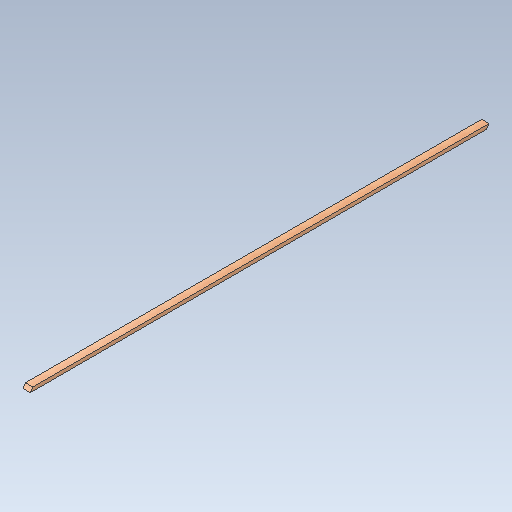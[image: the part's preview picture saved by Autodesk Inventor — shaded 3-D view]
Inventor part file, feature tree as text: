
AUTODESK INVENTOR PART (.ipt)
format: ipt  version: 2020.1 (Build 241239000, 239)  size: 265,216 bytes
history: native  units: mm
features: extrude x8, sketch x8, projected_geometry x7, other x7, fillet x4, reference x3
ambient origin geometry x8: Origin, YZ Plane, XZ Plane, XY Plane, X Axis, Y Axis, Z Axis, Center Point
bodies: Solid1 (feature_tree)
feature tree (37):
  extrude  "brædt"  Depth=80.0mm
  extrude  "spor til stål-håndfang"  Depth=40.0mm
  extrude  "spor til LED og liste"  Depth=4844.551mm
  extrude  "spor til ledninger"  Depth=5.0mm TaperAngle=0.0deg
  extrude  "endeafskær top"  Depth=6.3mm
  extrude  "endeafskær bund"  Depth=12.0mm TaperAngle=0.0deg
  fillet  "Fillet2"  Radius=1.0mm
  fillet  "Fillet3"  Radius=1.0mm
  fillet  "Fillet4"  Radius=10.0mm
  fillet  "Fillet5"  [1 undecoded]
  extrude  "pilothuller"  Depth=7.0mm TaperAngle=0.0deg
  extrude  "spor til acryl"  Depth=2.0mm
  sketch  "Sketch1"  dims[d5=5000.0mm d6=0.0mm d8=80.0mm]
  sketch  "Sketch2"  dims[d9=40.0mm d11=40.0mm]
  projected_geometry  "Projected Loop1"
  sketch  "Sketch3"  dims[d12=61.5mm d13=4844.551mm]
  projected_geometry  "Projected Loop2"
  sketch  "Sketch4"  dims[d14=3.0mm d15=5.0mm d16=0.0mm]
  projected_geometry  "Projected Loop3"
  sketch  "Sketch5"  dims[d17=9.5mm d18=6.3mm]
  projected_geometry  "Projected Loop4"
  sketch  "Sketch6"  dims[d19=12.0mm d20=12.0mm d21=0.0mm d22=1.0mm d23=1.0mm d24=10.0mm d25=0.0mm]
  projected_geometry  "Projected Loop5"
  sketch  "Sketch7"  dims[d26=0.0mm d27=7.0mm d28=0.0mm]
  reference  "Reference1"
  reference  "Reference2"
  reference  "Reference3"
  projected_geometry  "Projected Loop6"
  sketch  "Sketch8"  dims[d29=69.175mm d30=5.986479mm d31=7.0mm d32=0.0mm d33=5.986479mm d34=7.0mm d35=0.0mm d36=9.5mm d37=9.5mm d38=12.0mm d39=12.0mm d40=12.0mm d41=12.0mm d42=12.0mm d43=12.0mm d44=7.0mm d45=0.0mm d46=24.0mm d47=3.0mm d50=2.0mm d51=0.0mm d52=0.0mm d53=0.0mm]
  projected_geometry  "Projected Loop7"
  parser-record x1  (decoder bookkeeping rows leaked as tree rows — omitted from the tree; the rows remain in map.json)
  other  "søjle+vange.iam"
  other  "modul top:1"
  other  "stilladssøjle:1"
  other  "rør:1"
  other  "modul:1"
  other  "modul:2"
note: 1 required parameter value undecoded (feature->parameter linkage not recoverable at this tier; creation-order binding heuristic only, values carry confidence <= 0.55)
note: 1 file-system path scrubbed to <path> (originals preserved in map.json)
